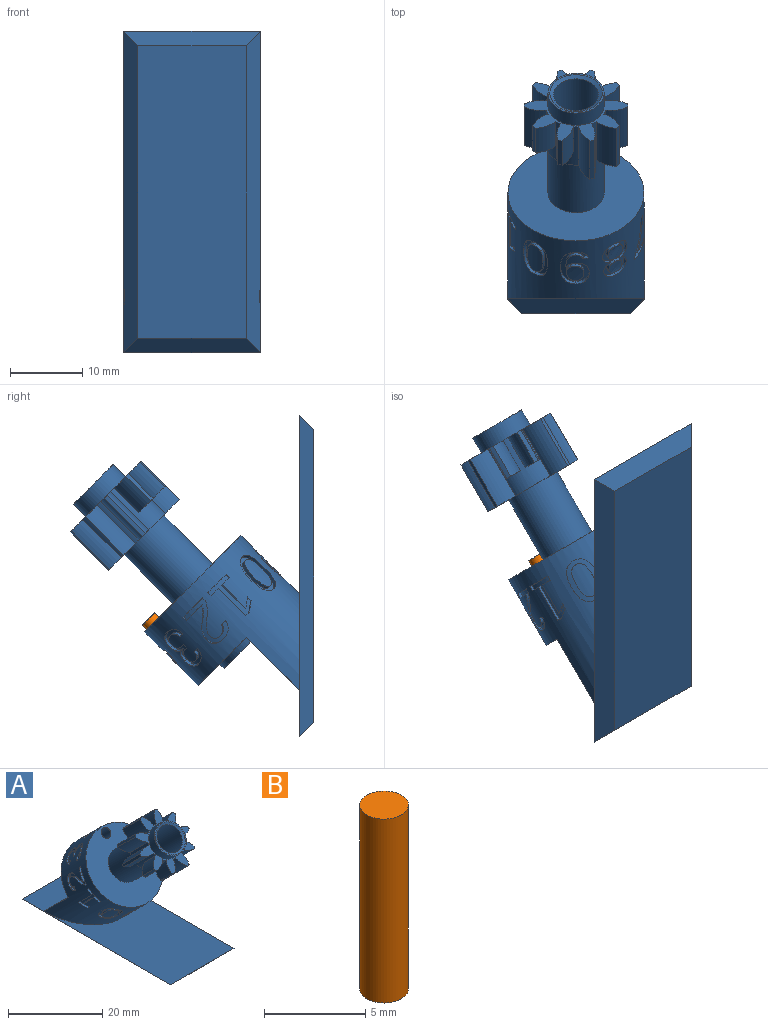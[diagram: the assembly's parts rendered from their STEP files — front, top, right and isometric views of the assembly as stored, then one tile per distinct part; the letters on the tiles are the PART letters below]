
ASSEMBLY  parts=2 mates=1
PART A: 299 faces, bbox 19.1x44.8x38.5 mm
  f0: cylinder r=9.45mm len=28.12mm, axis (0,0.71,-0.71), area 620.5mm2, adj f2,f4,f53,f54,f62,f63,f64,f65
  f1: cylinder r=5.25mm len=14.76mm, axis (0,0.71,-0.71), area 130.8mm2, adj f5,f6,f8,f53,f293
  f2: plane 7.34x7.34mm, normal (0,0.71,0.71), area 5.2mm2, adj f0,f3,f53,f293
  f3: cylinder r=8.95mm len=17.9mm, axis (0,-0.71,0.71), area 131.5mm2, adj f2,f4,f53,f293
  f4: plane 7.34x7.34mm, normal (0,0.71,0.71), area 5.2mm2, adj f0,f3,f53,f293
  f5: plane 6.7x6.7mm, normal (0,0.71,0.71), area 2.8mm2, adj f1,f7,f8,f293
  f6: plane 6.7x6.7mm, normal (0,0.71,0.71), area 2.8mm2, adj f1,f7,f8,f293
  f7: cylinder r=4.95mm len=10.2mm, axis (0,-0.71,0.71), area 98.3mm2, adj f5,f6,f8,f293
  f8: plane 10.5x7.21mm, normal (0,0.71,-0.71), area 26.4mm2, adj f1,f5,f6,f7,f52
  f9: plane 14.4x9.81mm, normal (0,0.71,-0.71), area 46.7mm2, adj f10,f11,f12,f19,f20,f21,f22,f23
  f10: cylinder r=4.5mm len=5.77mm, axis (0,0.71,-0.71), area 24.1mm2, adj f9,f11,f47,f48
  f11: cylinder r=7.2mm len=5.75mm, axis (0,0.71,-0.71), area 4.8mm2, adj f9,f10,f12,f48
  f12: cylinder r=4.5mm len=5.77mm, axis (0,0.71,-0.71), area 24.1mm2, adj f9,f11,f19,f48
  f13: cylinder r=4.5mm len=5.02mm, axis (0,0.71,-0.71), area 15.4mm2, adj f14,f19,f48,f50
  f14: cylinder r=7.2mm len=3.76mm, axis (0,0.71,-0.71), area 3.1mm2, adj f13,f15,f48,f50
  f15: cylinder r=4.5mm len=4.34mm, axis (0,0.71,-0.71), area 15.4mm2, adj f14,f19,f48,f50
  f16: cylinder r=4.5mm len=5.6mm, axis (0,0.71,-0.71), area 15.4mm2, adj f17,f19,f48,f49
  f17: cylinder r=7.2mm len=3.53mm, axis (0,0.71,-0.71), area 3.1mm2, adj f16,f18,f48,f49
  f18: cylinder r=4.5mm len=5.34mm, axis (0,0.71,-0.71), area 15.4mm2, adj f17,f19,f48,f49
  f19: cylinder r=4.2mm len=7.63mm, axis (0,0.71,-0.71), area 28mm2, adj f9,f12,f13,f15,f16,f18,f20,f48
  f20: cylinder r=4.5mm len=7.25mm, axis (0,0.71,-0.71), area 24.1mm2, adj f9,f19,f21,f48
  f21: cylinder r=7.2mm len=5.44mm, axis (0,0.71,-0.71), area 4.8mm2, adj f9,f20,f22,f48
  f22: cylinder r=4.5mm len=7.51mm, axis (0,0.71,-0.71), area 24.1mm2, adj f9,f21,f23,f48
  f23: cylinder r=4.2mm len=5.64mm, axis (0,0.71,-0.71), area 6mm2, adj f9,f22,f24,f48
  f24: cylinder r=4.5mm len=6.25mm, axis (0,0.71,-0.71), area 24.1mm2, adj f9,f23,f25,f48
  f25: cylinder r=7.2mm len=5.67mm, axis (0,0.71,-0.71), area 4.8mm2, adj f9,f24,f26,f48
  f26: cylinder r=4.5mm len=6.93mm, axis (0,0.71,-0.71), area 24.1mm2, adj f9,f25,f27,f48
  f27: cylinder r=4.2mm len=5.84mm, axis (0,0.71,-0.71), area 6mm2, adj f9,f26,f28,f48
  f28: cylinder r=4.5mm len=5.77mm, axis (0,0.71,-0.71), area 24.1mm2, adj f9,f27,f29,f48
  f29: cylinder r=7.2mm len=5.75mm, axis (0,0.71,-0.71), area 4.8mm2, adj f9,f28,f30,f48
  f30: cylinder r=4.5mm len=5.77mm, axis (0,0.71,-0.71), area 24.1mm2, adj f9,f29,f31,f48
  f31: cylinder r=4.2mm len=5.84mm, axis (0,0.71,-0.71), area 6mm2, adj f9,f30,f32,f48
  f32: cylinder r=4.5mm len=6.93mm, axis (0,0.71,-0.71), area 24.1mm2, adj f9,f31,f33,f48
  f33: cylinder r=7.2mm len=5.67mm, axis (0,0.71,-0.71), area 4.8mm2, adj f9,f32,f34,f48
  f34: cylinder r=4.5mm len=6.25mm, axis (0,0.71,-0.71), area 24.1mm2, adj f9,f33,f35,f48
  f35: cylinder r=4.2mm len=5.64mm, axis (0,0.71,-0.71), area 6mm2, adj f9,f34,f36,f48
  f36: cylinder r=4.5mm len=7.51mm, axis (0,0.71,-0.71), area 24.1mm2, adj f9,f35,f37,f48
  f37: cylinder r=7.2mm len=5.44mm, axis (0,0.71,-0.71), area 4.8mm2, adj f9,f36,f38,f48
  f38: cylinder r=4.5mm len=7.25mm, axis (0,0.71,-0.71), area 24.1mm2, adj f9,f37,f39,f48
  f39: cylinder r=4.2mm len=5.32mm, axis (0,0.71,-0.71), area 6mm2, adj f9,f38,f40,f48
  f40: cylinder r=4.5mm len=7.25mm, axis (0,0.71,-0.71), area 24.1mm2, adj f9,f39,f41,f48
  f41: cylinder r=7.2mm len=5.44mm, axis (0,0.71,-0.71), area 4.8mm2, adj f9,f40,f42,f48
  f42: cylinder r=4.5mm len=7.51mm, axis (0,0.71,-0.71), area 24.1mm2, adj f9,f41,f43,f48
  f43: cylinder r=4.2mm len=5.64mm, axis (0,0.71,-0.71), area 6mm2, adj f9,f42,f44,f48
  f44: cylinder r=4.5mm len=6.25mm, axis (0,0.71,-0.71), area 24.1mm2, adj f9,f43,f45,f48
  f45: cylinder r=7.2mm len=5.67mm, axis (0,0.71,-0.71), area 4.8mm2, adj f9,f44,f46,f48
  f46: cylinder r=4.5mm len=6.93mm, axis (0,0.71,-0.71), area 24.1mm2, adj f9,f45,f47,f48
  f47: cylinder r=4.2mm len=5.84mm, axis (0,0.71,-0.71), area 6mm2, adj f9,f10,f46,f48
  f48: plane 14.4x9.81mm, normal (0,-0.71,0.71), area 56.4mm2, adj f10,f11,f12,f13,f14,f15,f16,f17
  f49: plane 2.35x2.35mm, normal (0,0.71,-0.71), area 4.9mm2, adj f16,f17,f18,f19
  f50: plane 3.22x1.99mm, normal (0,0.71,-0.71), area 4.9mm2, adj f13,f14,f15,f19
  f51: cylinder r=3.9mm len=12.3mm, axis (0,0.71,-0.71), area 235.2mm2, adj f9,f54
  f52: cone r=3.12mm half-angle=30deg, axis (0,0.71,-0.71), area 49.7mm2, adj f8,f57
  f53: plane 18.9x13.01mm, normal (0,0.71,-0.71), area 175mm2, adj f0,f1,f2,f3,f4,f58
  f54: plane 18.9x13.36mm, normal (0,-0.71,0.71), area 228.2mm2, adj f0,f51,f58
  f55: cylinder r=3.9mm len=7.8mm, axis (0,0.71,-0.71), area 58.8mm2, adj f48,f56
  f56: plane 7.8x5.52mm, normal (0,-0.71,0.71), area 6.2mm2, adj f55,f59
  f57: cylinder r=3.12mm len=24.73mm, axis (0,0.71,-0.71), area 563.2mm2, adj f52,f59
  f58: cylinder r=1.2mm len=9.12mm, axis (0,-0.71,0.71), area 77.2mm2, adj f53,f54,f60,f61,f62,f63,f64,f65
  f59: cone r=3.64mm half-angle=60deg, axis (0,-0.71,0.71), area 12.7mm2, adj f56,f57
  f60: cylinder r=8.95mm len=4.38mm, axis (0,0.71,-0.71), area 4mm2, adj f58,f62,f66,f73,f74,f75,f76,f77
  f61: cylinder r=8.95mm len=2.98mm, axis (0,0.71,-0.71), area 3.2mm2, adj f58,f64,f65,f67,f71,f72,f79,f80
  f62: plane 0.74x0.39mm, normal (0,0.71,-0.71), area 0.4mm2, adj f0,f58,f60,f63,f75
  f63: plane 1.29x1.29mm, normal (1,0.02,0.02), area 0.6mm2, adj f0,f58,f62,f64
  f64: plane 2.84x0.57mm, normal (0,0.71,-0.71), area 1.4mm2, adj f0,f58,f61,f63,f72,f78
  f65: plane 3.46x2.95mm, normal (0.83,-0.38,0.41), area 2.4mm2, adj f0,f58,f61,f66,f72,f78
  f66: plane 0.82x0.39mm, normal (0,-0.71,0.71), area 0.4mm2, adj f0,f58,f60,f65,f76
  f67: plane 2.07x1.83mm, normal (-0.83,0.38,-0.41), area 1.4mm2, adj f58,f61,f68,f80,f138
  f68: extruded ~0.53x0.52mm, area 0.1mm2, adj f58,f67,f69,f138
  f69: extruded ~0.5x0.49mm, area 0.1mm2, adj f58,f68,f70,f138
  f70: plane 2.58x2.58mm, normal (1,0.02,0.02), area 1.5mm2, adj f58,f69,f71,f138
  f71: plane 2.13x0.5mm, normal (0,-0.71,0.71), area 1mm2, adj f58,f61,f70,f79,f138
  f72: plane 0.75x0.74mm, normal (-0.02,0.71,0.71), area 0.3mm2, adj f61,f64,f65,f78
  f73: plane 0.79x0.79mm, normal (-1,-0.02,-0.02), area 0.3mm2, adj f0,f60,f74,f77
  f74: plane 0.86x0.45mm, normal (0,0.71,-0.71), area 0.4mm2, adj f0,f60,f73,f75
  f75: plane 1.32x1.32mm, normal (-1,-0.02,-0.02), area 0.7mm2, adj f0,f60,f62,f74
  f76: plane 3.22x3.22mm, normal (-1,-0.02,-0.02), area 2mm2, adj f0,f60,f66,f77
  f77: plane 0.86x0.45mm, normal (0,-0.71,0.71), area 0.4mm2, adj f0,f60,f73,f76
  f78: plane 0.73x0.73mm, normal (1,0.02,0.02), area 0.3mm2, adj f0,f64,f65,f72
  f79: plane 0.43x0.41mm, normal (-0.78,0.43,-0.46), area 0.1mm2, adj f61,f71,f80,f138
  f80: plane 0.61x0.55mm, normal (-0.81,0.4,-0.43), area 0.2mm2, adj f61,f67,f79,f138
  f81: cylinder r=8.95mm len=6.17mm, axis (0,0.71,-0.71), area 9.9mm2, adj f82,f83,f84,f85,f86,f87,f88,f89
  f82: plane 0.31x0.29mm, normal (-0.78,-0.44,-0.44), area 0mm2, adj f0,f81,f83,f110
  f83: extruded ~1.11x1.09mm, area 0.5mm2, adj f0,f81,f82,f84
  f84: extruded ~1.12x0.84mm, area 0.5mm2, adj f0,f81,f83,f85
  f85: extruded ~1.38x0.94mm, area 0.7mm2, adj f0,f81,f84,f86
  f86: extruded ~1.47x1.24mm, area 0.8mm2, adj f0,f81,f85,f87
  f87: extruded ~1.45x1.23mm, area 0.7mm2, adj f0,f81,f86,f88
  f88: extruded ~1.43x0.9mm, area 0.7mm2, adj f0,f81,f87,f89,f112
  f89: plane 0.83x0.74mm, normal (0.06,0.74,-0.67), area 0.4mm2, adj f0,f81,f88,f90,f112
  f90: extruded ~0.99x0.66mm, area 0.4mm2, adj f0,f81,f89,f91
  f91: extruded ~0.99x0.85mm, area 0.4mm2, adj f0,f81,f90,f92
  f92: extruded ~0.99x0.86mm, area 0.5mm2, adj f0,f81,f91,f93
  f93: extruded ~0.96x0.71mm, area 0.4mm2, adj f0,f81,f92,f94
  f94: extruded ~0.99x0.68mm, area 0.4mm2, adj f0,f81,f93,f95
  f95: extruded ~1.09x0.91mm, area 0.5mm2, adj f0,f81,f94,f96
  f96: plane 0.62x0.48mm, normal (0,-0.71,0.71), area 0.2mm2, adj f0,f81,f95,f97
  f97: plane 0.75x0.75mm, normal (0.78,0.44,0.44), area 0.3mm2, adj f0,f81,f96,f98
  f98: plane 0.64x0.48mm, normal (0,0.71,-0.71), area 0.2mm2, adj f0,f81,f97,f99
  f99: extruded ~1.18x0.97mm, area 0.6mm2, adj f0,f81,f98,f100
  f100: extruded ~1.01x0.68mm, area 0.4mm2, adj f0,f81,f99,f101
  f101: extruded ~1.04x0.75mm, area 0.5mm2, adj f0,f81,f100,f102
  f102: extruded ~1.05x0.9mm, area 0.5mm2, adj f0,f81,f101,f103
  f103: extruded ~1.67x1.41mm, area 0.9mm2, adj f0,f81,f102,f104
  f104: plane 0.84x0.76mm, normal (0.07,-0.66,0.74), area 0.4mm2, adj f0,f81,f103,f105,f111
  f105: extruded ~1.49x0.92mm, area 0.7mm2, adj f0,f81,f104,f106,f111
  f106: extruded ~1.54x1.28mm, area 0.8mm2, adj f0,f81,f105,f107
  f107: extruded ~1.57x1.33mm, area 0.8mm2, adj f0,f81,f106,f108
  f108: extruded ~1.48x1.02mm, area 0.7mm2, adj f0,f81,f107,f109
  f109: extruded ~1.16x0.83mm, area 0.5mm2, adj f0,f81,f108,f110
  f110: extruded ~1.21x1.13mm, area 0.6mm2, adj f0,f81,f82,f109
  f111: plane 0.39x0.35mm, normal (-0.62,0.55,0.55), area 0mm2, adj f81,f104,f105
  f112: plane 0.04x0.04mm, normal (-0.62,0.55,0.55), area 0mm2, adj f81,f88,f89
  f113: cylinder r=8.95mm len=7.04mm, axis (0,0.71,-0.71), area 8.9mm2, adj f114,f115,f116,f117,f118,f119,f120,f121
  f114: plane 2.21x2.21mm, normal (0,-0.71,0.71), area 1.6mm2, adj f0,f113,f115,f137
  f115: extruded ~0.83x0.64mm, area 0.4mm2, adj f0,f113,f114,f116
  f116: extruded ~1.15x0.72mm, area 0.5mm2, adj f0,f113,f115,f117
  f117: extruded ~1.69x0.88mm, area 0.8mm2, adj f0,f113,f116,f118
  f118: extruded ~0.92x0.69mm, area 0.4mm2, adj f0,f113,f117,f119
  f119: extruded ~0.7x0.56mm, area 0.4mm2, adj f0,f113,f118,f120
  f120: extruded ~1.31x0.7mm, area 0.7mm2, adj f0,f113,f119,f121
  f121: extruded ~1.37x0.95mm, area 0.8mm2, adj f0,f113,f120,f122
  f122: extruded ~1.34x0.95mm, area 0.7mm2, adj f0,f113,f121,f123
  f123: extruded ~1.35x0.77mm, area 0.7mm2, adj f0,f113,f122,f124
  f124: plane 0.71x0.61mm, normal (0.02,0.77,-0.64), area 0.4mm2, adj f0,f113,f123,f125
  f125: extruded ~0.89x0.63mm, area 0.4mm2, adj f0,f113,f124,f126
  f126: extruded ~0.84x0.74mm, area 0.4mm2, adj f0,f113,f125,f127
  f127: extruded ~0.84x0.72mm, area 0.4mm2, adj f0,f113,f126,f128
  f128: extruded ~0.84x0.59mm, area 0.4mm2, adj f0,f113,f127,f129
  f129: extruded ~0.68x0.55mm, area 0.3mm2, adj f0,f113,f128,f130
  f130: extruded ~0.79x0.63mm, area 0.4mm2, adj f0,f113,f129,f131
  f131: extruded ~0.89x0.65mm, area 0.4mm2, adj f0,f113,f130,f132
  f132: extruded ~0.97x0.7mm, area 0.4mm2, adj f0,f113,f131,f133
  f133: extruded ~1.05x0.75mm, area 0.5mm2, adj f0,f113,f132,f134
  f134: extruded ~1.1x0.74mm, area 0.5mm2, adj f0,f113,f133,f135
  f135: plane 0.5x0.48mm, normal (0.26,0.68,0.68), area 0.3mm2, adj f0,f113,f134,f136
  f136: plane 2.82x2.82mm, normal (0,0.71,-0.71), area 2mm2, adj f0,f113,f135,f137
  f137: plane 0.56x0.56mm, normal (-0.26,-0.68,-0.68), area 0.3mm2, adj f0,f113,f114,f136
  f138: cylinder r=9.45mm len=2.39mm, axis (0,0.71,-0.71), area 3.3mm2, adj f67,f68,f69,f70,f71,f79,f80
  f139: cylinder r=8.95mm len=5.96mm, axis (0,0.71,-0.71), area 9.8mm2, adj f140,f141,f142,f143,f144,f145,f146,f147
  f140: extruded ~1.35x1.12mm, area 0.7mm2, adj f0,f139,f141,f160
  f141: plane 1.68x1.6mm, normal (-0.81,0.45,0.37), area 1mm2, adj f0,f139,f140,f142
  f142: plane 2.46x1.45mm, normal (0,0.71,-0.71), area 1.4mm2, adj f0,f139,f141,f143
  f143: plane 0.75x0.75mm, normal (-0.81,0.41,0.41), area 0.3mm2, adj f0,f139,f142,f144
  f144: plane 3.1x1.68mm, normal (0,-0.71,0.71), area 1.7mm2, adj f0,f139,f143,f145
  f145: plane 2.65x2.53mm, normal (0.81,-0.45,-0.37), area 1.7mm2, adj f0,f139,f144,f146
  f146: plane 0.99x0.52mm, normal (0,0.71,-0.71), area 0.4mm2, adj f0,f139,f145,f147
  f147: extruded ~0.78x0.77mm, area 0.3mm2, adj f0,f139,f146,f148
  f148: extruded ~0.78x0.61mm, area 0.3mm2, adj f0,f139,f147,f149
  f149: extruded ~1.08x0.95mm, area 0.5mm2, adj f0,f139,f148,f150
  f150: extruded ~1.11x0.82mm, area 0.5mm2, adj f0,f139,f149,f151
  f151: extruded ~1.18x0.89mm, area 0.6mm2, adj f0,f139,f150,f152
  f152: extruded ~1.1x0.97mm, area 0.5mm2, adj f0,f139,f151,f153
  f153: extruded ~1.5x1.37mm, area 0.8mm2, adj f0,f139,f152,f154
  f154: plane 1.01x0.59mm, normal (0.09,-0.75,0.65), area 0.4mm2, adj f0,f139,f153,f155,f161
  f155: extruded ~1.38x0.89mm, area 0.7mm2, adj f0,f139,f154,f156,f161
  f156: extruded ~1.47x1.18mm, area 0.7mm2, adj f0,f139,f155,f157
  f157: extruded ~1.63x1.38mm, area 0.9mm2, adj f0,f139,f156,f158
  f158: extruded ~1.64x1.18mm, area 0.8mm2, adj f0,f139,f157,f159
  f159: extruded ~1.53x1.09mm, area 0.8mm2, adj f0,f139,f158,f160
  f160: extruded ~1.51x1.3mm, area 0.8mm2, adj f0,f139,f140,f159
  f161: plane 0.29x0.26mm, normal (0.58,0.57,0.57), area 0mm2, adj f139,f154,f155
  f162: cylinder r=8.95mm len=7.09mm, axis (0,0.71,-0.71), area 10.3mm2, adj f163,f164,f165,f166,f167,f168,f169,f170
  f163: extruded ~1.39x0.99mm, area 0.7mm2, adj f0,f162,f164,f177
  f164: extruded ~1.45x0.79mm, area 0.8mm2, adj f0,f162,f163,f165
  f165: extruded ~1.54x0.85mm, area 0.8mm2, adj f0,f162,f164,f166
  f166: extruded ~1.48x1.02mm, area 0.8mm2, adj f0,f162,f165,f167
  f167: extruded ~1.72x1.08mm, area 0.9mm2, adj f0,f162,f166,f168
  f168: extruded ~2.05x1.33mm, area 1.2mm2, adj f0,f162,f167,f169
  f169: extruded ~2.21x1.46mm, area 1.3mm2, adj f0,f162,f168,f170
  f170: extruded ~1.8x1.09mm, area 0.9mm2, adj f0,f162,f169,f171
  f171: extruded ~2.17x1.17mm, area 1.2mm2, adj f0,f162,f170,f172
  f172: plane 0.72x0.6mm, normal (-0.05,0.82,-0.58), area 0.4mm2, adj f0,f162,f171,f173
  f173: extruded ~1.31x0.84mm, area 0.7mm2, adj f0,f162,f172,f174
  f174: extruded ~1.24x0.84mm, area 0.6mm2, adj f0,f162,f173,f175
  f175: extruded ~1.62x1.13mm, area 0.9mm2, adj f0,f162,f174,f176
  f176: extruded ~0.94x0.72mm, area 0.4mm2, adj f0,f162,f175,f177
  f177: extruded ~0.84x0.77mm, area 0.5mm2, adj f0,f162,f163,f176
  f178: extruded ~1.03x0.79mm, area 0.5mm2, adj f162,f179,f185,f289
  f179: extruded ~1.15x0.69mm, area 0.6mm2, adj f162,f178,f180,f289
  f180: extruded ~0.95x0.62mm, area 0.5mm2, adj f162,f179,f181,f289
  f181: extruded ~0.93x0.79mm, area 0.5mm2, adj f162,f180,f182,f289
  f182: extruded ~0.97x0.79mm, area 0.5mm2, adj f162,f181,f183,f289
  f183: extruded ~1.04x0.61mm, area 0.5mm2, adj f162,f182,f184,f289
  f184: extruded ~1.05x0.63mm, area 0.6mm2, adj f162,f183,f185,f289
  f185: extruded ~0.97x0.78mm, area 0.5mm2, adj f162,f178,f184,f289
  f186: cylinder r=8.95mm len=6.93mm, axis (0,0.71,-0.71), area 6.5mm2, adj f187,f188,f189,f190,f191,f192,f193,f194
  f187: plane 0.58x0.58mm, normal (-0.32,-0.67,-0.67), area 0.3mm2, adj f0,f186,f188,f196
  f188: plane 2.32x2.32mm, normal (0,0.71,-0.71), area 1.6mm2, adj f0,f186,f187,f189
  f189: extruded ~3.3x1.11mm, area 1.7mm2, adj f0,f186,f188,f190
  f190: extruded ~2.17x1.51mm, area 1.2mm2, adj f0,f186,f189,f191
  f191: plane 0.69x0.66mm, normal (0,0.71,-0.71), area 0.4mm2, adj f0,f186,f190,f192
  f192: extruded ~1.38x1.12mm, area 0.8mm2, adj f0,f186,f191,f193
  f193: extruded ~1.61x0.85mm, area 0.8mm2, adj f0,f186,f192,f194
  f194: extruded ~2.59x1.07mm, area 1.3mm2, adj f0,f186,f193,f195
  f195: plane 0.56x0.56mm, normal (0.32,0.67,0.67), area 0.3mm2, adj f0,f186,f194,f196
  f196: plane 2.79x2.79mm, normal (0,-0.71,0.71), area 2mm2, adj f0,f186,f187,f195
  f197: cylinder r=8.95mm len=6.04mm, axis (0,0.71,-0.71), area 11.8mm2, adj f198,f199,f200,f201,f202,f203,f204,f205
  f198: plane 0.73x0.73mm, normal (0.57,-0.58,-0.58), area 0mm2, adj f197,f204,f205
  f199: extruded ~1.09x1.07mm, area 0.5mm2, adj f0,f197,f200,f216
  f200: extruded ~1.16x0.9mm, area 0.5mm2, adj f0,f197,f199,f201
  f201: extruded ~1.48x1.06mm, area 0.7mm2, adj f0,f197,f200,f202
  f202: extruded ~1.6x1.3mm, area 0.8mm2, adj f0,f197,f201,f203
  f203: extruded ~1.61x1.31mm, area 0.8mm2, adj f0,f197,f202,f204
  f204: extruded ~1.49x1.05mm, area 0.8mm2, adj f0,f197,f198,f203,f205
  f205: extruded ~1.17x0.9mm, area 0.6mm2, adj f0,f197,f198,f204,f206
  f206: extruded ~1.07x1.06mm, area 0.5mm2, adj f0,f197,f205,f207
  f207: plane 0.3x0.3mm, normal (-0.82,-0.41,-0.41), area 0mm2, adj f0,f197,f206,f208
  f208: extruded ~1.03x0.99mm, area 0.5mm2, adj f0,f197,f207,f209
  f209: extruded ~1.08x0.85mm, area 0.5mm2, adj f0,f197,f208,f210
  f210: extruded ~1.35x0.93mm, area 0.6mm2, adj f0,f197,f209,f211
  f211: extruded ~1.49x1.23mm, area 0.7mm2, adj f0,f197,f210,f212
  f212: extruded ~1.49x1.21mm, area 0.8mm2, adj f0,f197,f211,f213
  f213: extruded ~1.35x0.94mm, area 0.7mm2, adj f0,f197,f212,f214
  f214: extruded ~1.08x0.85mm, area 0.5mm2, adj f0,f197,f213,f215
  f215: extruded ~1.01x0.98mm, area 0.5mm2, adj f0,f197,f214,f216
  f216: plane 0.3x0.3mm, normal (0.82,0.41,0.41), area 0mm2, adj f0,f197,f199,f215
  f217: extruded ~0.98x0.82mm, area 0.4mm2, adj f197,f218,f223,f231
  f218: extruded ~0.99x0.76mm, area 0.4mm2, adj f197,f217,f219,f231
  f219: extruded ~1.5x1.24mm, area 0.9mm2, adj f197,f218,f220,f231
  f220: extruded ~0.99x0.84mm, area 0.4mm2, adj f197,f219,f221,f231
  f221: extruded ~0.97x0.74mm, area 0.4mm2, adj f197,f220,f222,f231
  f222: extruded ~0.99x0.75mm, area 0.4mm2, adj f197,f221,f223,f231
  f223: extruded ~0.99x0.85mm, area 0.4mm2, adj f197,f217,f222,f231
  f224: extruded ~1.74x1.39mm, area 1mm2, adj f197,f225,f230,f290
  f225: extruded ~1.04x0.78mm, area 0.5mm2, adj f197,f224,f226,f290
  f226: extruded ~1.07x0.91mm, area 0.5mm2, adj f197,f225,f227,f290
  f227: extruded ~1.07x0.89mm, area 0.5mm2, adj f197,f226,f228,f290
  f228: extruded ~1.04x0.77mm, area 0.5mm2, adj f197,f227,f229,f290
  f229: extruded ~1.11x0.86mm, area 0.5mm2, adj f197,f228,f230,f290
  f230: extruded ~1.07x0.9mm, area 0.5mm2, adj f197,f224,f229,f290
  f231: cylinder r=9.45mm len=2.39mm, axis (0,0.71,-0.71), area 3.2mm2, adj f217,f218,f219,f220,f221,f222,f223
  f232: cylinder r=8.95mm len=4.57mm, axis (0,0.71,-0.71), area 10.5mm2, adj f233,f234,f235,f236,f237,f238,f239,f240
  f233: plane 0.48x0.48mm, normal (-0.03,-0.71,-0.71), area 0mm2, adj f232,f247,f248
  f234: extruded ~1.54x0.99mm, area 0.9mm2, adj f0,f232,f235,f249
  f235: extruded ~2.02x2mm, area 1.2mm2, adj f0,f232,f234,f236
  f236: extruded ~2.13x2.11mm, area 1.3mm2, adj f0,f232,f235,f237
  f237: extruded ~1.63x1.04mm, area 1mm2, adj f0,f232,f236,f238
  f238: extruded ~1.15x0.66mm, area 0.6mm2, adj f0,f232,f237,f239
  f239: extruded ~1.13x1.11mm, area 0.6mm2, adj f0,f232,f238,f240
  f240: plane 0.75x0.52mm, normal (-0.16,-0.7,0.7), area 0.4mm2, adj f0,f232,f239,f241
  f241: extruded ~1.03x0.97mm, area 0.7mm2, adj f0,f232,f240,f242
  f242: extruded ~1.04x0.83mm, area 0.6mm2, adj f0,f232,f241,f243
  f243: extruded ~1.63x1.62mm, area 0.9mm2, adj f0,f232,f242,f244
  f244: extruded ~0.84x0.82mm, area 0.4mm2, adj f0,f232,f243,f245
  f245: extruded ~0.92x0.54mm, area 0.5mm2, adj f0,f232,f244,f246
  f246: extruded ~1.31x0.87mm, area 0.7mm2, adj f0,f232,f245,f247
  f247: extruded ~1.48x1.46mm, area 0.8mm2, adj f0,f232,f233,f246,f248
  f248: extruded ~1.49x1.47mm, area 0.8mm2, adj f0,f232,f233,f247,f249
  f249: extruded ~1.49x0.86mm, area 0.8mm2, adj f0,f232,f234,f248
  f250: extruded ~0.63x0.48mm, area 0.3mm2, adj f232,f251,f258,f291
  f251: extruded ~0.88x0.68mm, area 0.5mm2, adj f232,f250,f252,f291
  f252: extruded ~1.13x1.12mm, area 0.6mm2, adj f232,f251,f253,f291
  f253: extruded ~1.11x1.1mm, area 0.6mm2, adj f232,f252,f254,f291
  f254: extruded ~0.89x0.68mm, area 0.5mm2, adj f232,f253,f255,f291
  f255: extruded ~0.91x0.7mm, area 0.5mm2, adj f232,f254,f256,f291
  f256: extruded ~1.21x1.2mm, area 0.6mm2, adj f232,f255,f257,f291
  f257: extruded ~0.82x0.81mm, area 0.3mm2, adj f232,f256,f258,f291
  f258: extruded ~0.69x0.67mm, area 0.3mm2, adj f232,f250,f257,f291
  f259: cylinder r=8.95mm len=6.13mm, axis (0,0.71,-0.71), area 9.9mm2, adj f260,f261,f262,f263,f264,f265,f266,f267
  f260: plane 1.9x1.9mm, normal (-0.62,-0.56,-0.56), area 0.2mm2, adj f259,f266,f267
  f261: extruded ~1.62x1.58mm, area 0.9mm2, adj f0,f259,f262,f268
  f262: extruded ~2.19x1.75mm, area 1.2mm2, adj f0,f259,f261,f263
  f263: extruded ~2.2x1.73mm, area 1.2mm2, adj f0,f259,f262,f264
  f264: extruded ~1.61x1.59mm, area 0.9mm2, adj f0,f259,f263,f265
  f265: extruded ~1.63x1.61mm, area 0.9mm2, adj f0,f259,f264,f266
  f266: extruded ~2.19x1.73mm, area 1.2mm2, adj f0,f259,f260,f265,f267
  f267: extruded ~2.19x1.75mm, area 1.2mm2, adj f0,f259,f260,f266,f268
  f268: extruded ~1.67x1.62mm, area 0.9mm2, adj f0,f259,f261,f267
  f269: extruded ~1.17x1.14mm, area 0.6mm2, adj f259,f270,f276,f292
  f270: extruded ~1.77x1.49mm, area 1mm2, adj f259,f269,f271,f292
  f271: extruded ~1.78x1.51mm, area 1mm2, adj f259,f270,f272,f292
  f272: extruded ~1.17x1.15mm, area 0.6mm2, adj f259,f271,f273,f292
  f273: extruded ~1.15x1.12mm, area 0.6mm2, adj f259,f272,f274,f292
  f274: extruded ~1.77x1.5mm, area 1mm2, adj f259,f273,f275,f292
  f275: extruded ~1.75x1.48mm, area 1mm2, adj f259,f274,f276,f292
  f276: extruded ~1.16x1.12mm, area 0.6mm2, adj f259,f269,f275,f292
  f277: cylinder r=8.95mm len=6.83mm, axis (0,0.71,-0.71), area 7.6mm2, adj f278,f279,f280,f281,f282,f283,f284,f285
  f278: plane 1.13x1.13mm, normal (0,-0.71,0.71), area 0.7mm2, adj f0,f277,f279,f288
  f279: plane 3.89x3.89mm, normal (0.26,-0.68,-0.68), area 2.7mm2, adj f0,f277,f278,f280
  f280: plane 0.66x0.58mm, normal (0,-0.71,0.71), area 0.4mm2, adj f0,f277,f279,f281
  f281: plane 1.73x1.01mm, normal (-0.15,-0.2,0.97), area 0.9mm2, adj f0,f277,f280,f282
  f282: plane 0.61x0.61mm, normal (-0.26,0.68,0.68), area 0.4mm2, adj f0,f277,f281,f283
  f283: plane 1.68x0.99mm, normal (0.15,0.18,-0.97), area 0.8mm2, adj f0,f277,f282,f284
  f284: plane 3.37x3.37mm, normal (-0.26,0.68,0.68), area 2.3mm2, adj f0,f277,f283,f285
  f285: plane 1.11x1.11mm, normal (0,-0.71,0.71), area 0.8mm2, adj f0,f277,f284,f286
  f286: plane 0.56x0.56mm, normal (-0.26,0.68,0.68), area 0.3mm2, adj f0,f277,f285,f287
  f287: plane 2.67x2.67mm, normal (0,0.71,-0.71), area 1.9mm2, adj f0,f277,f286,f288
  f288: plane 0.56x0.56mm, normal (0.26,-0.68,-0.68), area 0.3mm2, adj f0,f277,f278,f287
  f289: cylinder r=9.45mm len=3.58mm, axis (0,0.71,-0.71), area 4.9mm2, adj f178,f179,f180,f181,f182,f183,f184,f185
  f290: cylinder r=9.45mm len=2.72mm, axis (0,0.71,-0.71), area 4.1mm2, adj f224,f225,f226,f227,f228,f229,f230
  f291: cylinder r=9.45mm len=2.42mm, axis (0,0.71,-0.71), area 5mm2, adj f250,f251,f252,f253,f254,f255,f256,f257
  f292: cylinder r=9.45mm len=4.62mm, axis (0,0.71,-0.71), area 9.9mm2, adj f269,f270,f271,f272,f273,f274,f275,f276
  f293: plane 44.61x19mm, normal (0,0,1), area 820.3mm2, adj f0,f1,f2,f3,f4,f5,f6,f7
  f294: plane 40.61x15mm, normal (0,0,-1), area 609.1mm2, adj f295,f296,f297,f298
  f295: plane 19x2mm, normal (0,-0.71,-0.71), area 48.1mm2, adj f293,f294,f296,f297
  f296: plane 44.61x2mm, normal (0.71,0,-0.71), area 120.5mm2, adj f293,f294,f295,f298
  f297: plane 44.61x2mm, normal (-0.71,0,-0.71), area 120.5mm2, adj f293,f294,f295,f298
  f298: plane 19x2mm, normal (0,0.71,-0.71), area 48.1mm2, adj f293,f294,f296,f297
PART B: 3 faces, bbox 2.4x2.4x11.1 mm
  f0: cylinder r=1.2mm len=11.1mm, axis (0,0,-1), area 83.7mm2, adj f1,f2
  f1: plane 2.4x2.4mm, normal (0,0,1), area 4.5mm2, adj f0
  f2: plane 2.4x2.4mm, normal (0,0,-1), area 4.5mm2, adj f0
PLACE A rot(axis=(-1,0,0),90deg) t=(0,-5.2,-7.6)mm
PLACE B rot(axis=(-1,0,0),45deg) t=(0,1.16,-12.27)mm
MATE fastened B.f0 <-> A.f58  axis (0,0.71,0.71) through (0,9.01,-4.42)mm
